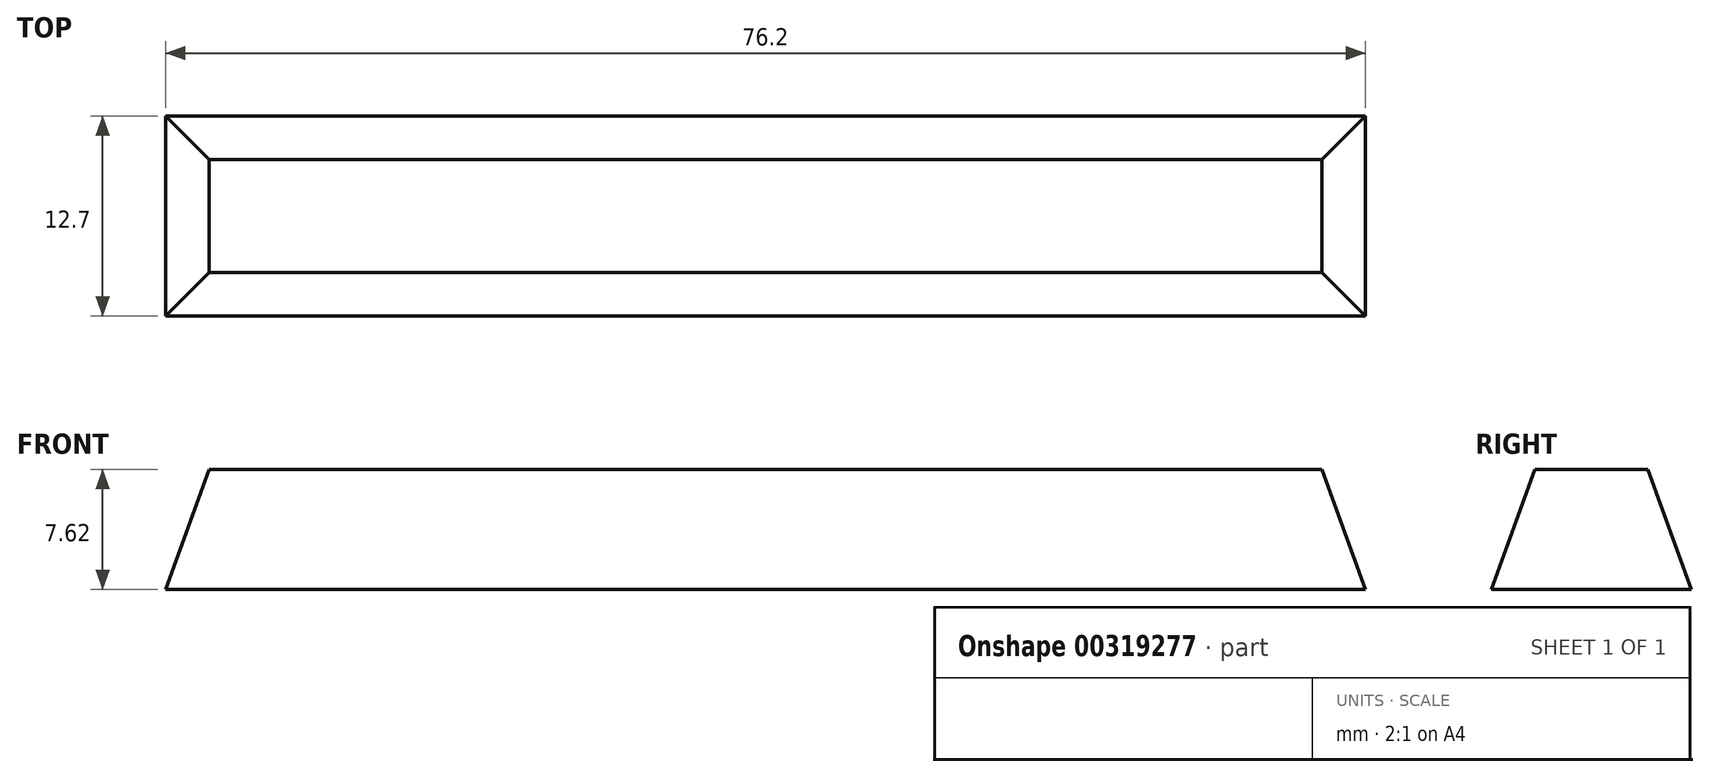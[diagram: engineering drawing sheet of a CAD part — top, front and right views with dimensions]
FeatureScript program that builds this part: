
annotation { "Feature Type Name" : "Feature", "Feature Type Description" : "" }
export const myFeature = defineFeature(function(context is Context, id is Id, definition is map)
    precondition{}
    {
        {
            var Q0;
            Q0=qCreatedBy(makeId("Top.planeOp"),FACE);
            var sketch = newSketch(context, id + "F0", { "sketchPlane" : qUnion([Q0])});
            skLineSegment(sketch, "E0.bottom", {"start": v(-31.6, 17.15) * mm, "end": v(44.6, 17.15) * mm});
            skLineSegment(sketch, "E0.top", {"start": v(-31.6, 4.45) * mm, "end": v(44.6, 4.45) * mm});
            skLineSegment(sketch, "E0.left", {"start": v(-31.6, 17.15) * mm, "end": v(-31.6, 4.45) * mm});
            skLineSegment(sketch, "E0.right", {"start": v(44.6, 17.15) * mm, "end": v(44.6, 4.45) * mm});
            skSolve(sketch);
        }
        {
            var Q0;
            Q0 = qSketchRegion(id + "F0", true);
            extrude(context, id + "F1", {"entities" : qUnion([Q0]), "depth" : 7.62 * mm, "hasDraft" : true, "draftAngle" : 20 * degree, "draftPullDirection" : true});
        }
    });
